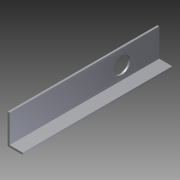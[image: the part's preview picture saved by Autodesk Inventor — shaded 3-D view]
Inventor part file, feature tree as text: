
AUTODESK INVENTOR PART (.ipt)
format: ipt  version: 2012 (Build 160160000, 160)  size: 86,016 bytes
history: native  units: in
note: dims shown in document units (in); Inventor stores cm internally (conversion verified against a paired STEP export)
features: extrude x2, sketch x2
ambient origin geometry x8: Origin, YZ Plane, XZ Plane, XY Plane, X Axis, Y Axis, Z Axis, Center Point
bodies: Solid1 (feature_tree)
feature tree (4):
  extrude  "Extrusion1"  Depth=1.0in
  extrude  "Extrusion2"  Depth=0.125in
  sketch  "Sketch1"  dims[d0=2.0in d1=1.0in]
  sketch  "Sketch2"  dims[d2=0.125in d3=0.125in d4=10.0in d5=0.0in d6=1.125in d7=2.5in d8=1.0in d9=4.0in d10=0.0in]
